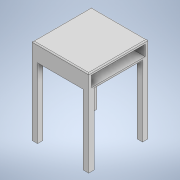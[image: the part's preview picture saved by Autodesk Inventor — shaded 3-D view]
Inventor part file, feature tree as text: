
AUTODESK INVENTOR PART (.ipt)
format: ipt  version: 2021 (Build 250183000, 183)  size: 150,016 bytes
history: native  units: in
note: dims shown in document units (in); Inventor stores cm internally (conversion verified against a paired STEP export)
features: extrude x3, sketch x3, other x1, fillet x1
ambient origin geometry x8: Origin, YZ Plane, XZ Plane, XY Plane, X Axis, Y Axis, Z Axis, Center Point
bodies: Body1 (feature_tree)
feature tree (8):
  other  "Sólido1"
  extrude  "Extrusión1"  Depth=4.3307in
  extrude  "Extrusión2"  Depth=4.3307in
  extrude  "Extrusión3"  Depth=0.1969in
  fillet  "Empalme1"  Radius=0.1969in
  sketch  "Boceto1"  dims[d0=2.1654in d1=4.3307in]
  sketch  "Boceto2"  dims[d2=4.1339in d3=4.3307in]
  sketch  "Boceto3"  dims[d4=1.1811in d5=0.0in d6=0.1969in d7=0.1969in d9=4.3307in d10=0.1969in d11=0.1969in d12=3.937in d13=0.0in d14=0.3937in d15=0.3937in d16=0.3937in d17=0.3937in d18=5.1181in d19=0.0in d20=0.0787in]
